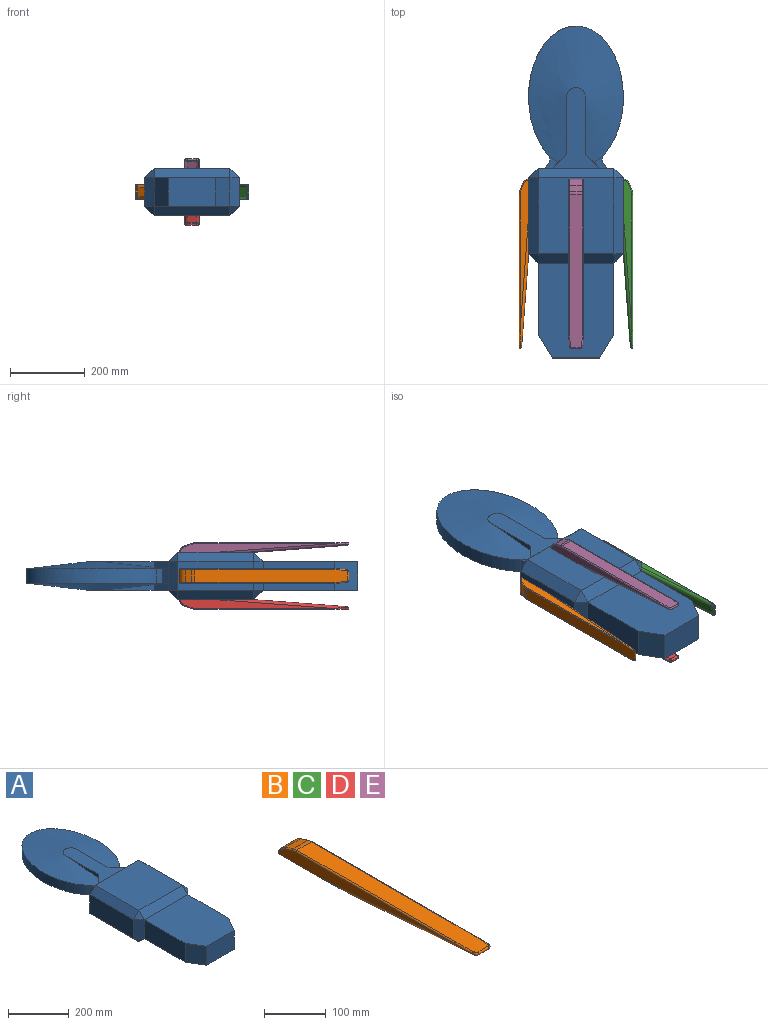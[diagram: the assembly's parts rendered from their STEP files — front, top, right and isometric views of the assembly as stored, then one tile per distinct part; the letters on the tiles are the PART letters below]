
ASSEMBLY  parts=5 mates=3
PART A: 54 faces, bbox 256.2x891.2x129.2 mm
  f0: plane 190.5x76.2mm, normal (1,0,0), area 14516.1mm2, adj f1,f3,f27,f53
  f1: plane 254x203.2mm, normal (0,0,1), area 49193.5mm2, adj f0,f2,f22,f51,f52,f53
  f2: plane 127x76.2mm, normal (0,-1,0), area 9677.4mm2, adj f1,f3,f52,f53
  f3: plane 254x203.2mm, normal (0,0,-1), area 49193.5mm2, adj f0,f2,f33,f51,f52,f53
  f4: plane 36.25x31.4mm, normal (0,0,1), area 482.6mm2, adj f9,f37,f38,f39,f50
  f5: plane 76.2x38.1mm, normal (0,1,0), area 2080.6mm2, adj f7,f8,f14,f18,f19,f34,f46,f49
  f6: plane 36.43x31.41mm, normal (0,0,-1), area 482.7mm2, adj f9,f37,f38,f41,f43
  f7: plane 36.43x31.41mm, normal (0,0,-1), area 482.6mm2, adj f5,f34,f35,f41,f46
  f8: plane 36.25x31.4mm, normal (0,0,1), area 482.7mm2, adj f5,f34,f35,f39,f49
  f9: plane 76.2x38.1mm, normal (0,1,0), area 2080.6mm2, adj f4,f6,f14,f19,f20,f38,f43,f50
  f10: plane 203.2x76.2mm, normal (1,0,0), area 15483.8mm2, adj f17,f18,f27,f28
  f11: plane 203.2x76.2mm, normal (-1,0,0), area 15483.8mm2, adj f20,f21,f29,f30
  f12: plane 203.2x203.2mm, normal (0,0,1), area 41290.2mm2, adj f14,f17,f21,f22
  f13: plane 203.2x203.2mm, normal (0,0,-1), area 41290.2mm2, adj f19,f28,f29,f33
  f14: plane 203.2x25.4mm, normal (0,0.71,0.71), area 7299.2mm2, adj f5,f9,f12,f15,f16,f40
  f15: plane 25.4x25.4mm, normal (0.58,0.58,0.58), area 558.7mm2, adj f14,f17,f18
  f16: plane 25.4x25.4mm, normal (-0.58,0.58,0.58), area 558.7mm2, adj f14,f20,f21
  f17: plane 203.2x25.4mm, normal (0.71,0,0.71), area 7299.2mm2, adj f10,f12,f15,f23
  f18: plane 76.2x25.4mm, normal (0.71,0.71,0), area 2737.2mm2, adj f5,f10,f15,f24
  f19: plane 203.2x25.4mm, normal (0,0.71,-0.71), area 7299.2mm2, adj f5,f9,f13,f24,f25,f42
  f20: plane 76.2x25.4mm, normal (-0.71,0.71,0), area 2737.2mm2, adj f9,f11,f16,f25
  f21: plane 203.2x25.4mm, normal (-0.71,0,0.71), area 7299.2mm2, adj f11,f12,f16,f26
  f22: plane 203.2x25.4mm, normal (0,-0.71,0.71), area 7299.2mm2, adj f1,f12,f23,f26
  f23: plane 25.4x25.4mm, normal (0.58,-0.58,0.58), area 558.7mm2, adj f17,f22,f27
  f24: plane 25.4x25.4mm, normal (0.58,0.58,-0.58), area 558.7mm2, adj f18,f19,f28
  f25: plane 25.4x25.4mm, normal (-0.58,0.58,-0.58), area 558.7mm2, adj f19,f20,f29
  f26: plane 25.4x25.4mm, normal (-0.58,-0.58,0.58), area 558.7mm2, adj f21,f22,f30
  f27: plane 76.2x25.4mm, normal (0.71,-0.71,0), area 2737.2mm2, adj f0,f10,f23,f31
  f28: plane 203.2x25.4mm, normal (0.71,0,-0.71), area 7299.2mm2, adj f10,f13,f24,f31
  f29: plane 203.2x25.4mm, normal (-0.71,0,-0.71), area 7299.2mm2, adj f11,f13,f25,f32
  f30: plane 76.2x25.4mm, normal (-0.71,-0.71,0), area 2737.2mm2, adj f11,f26,f32,f51
  f31: plane 25.4x25.4mm, normal (0.58,-0.58,-0.58), area 558.7mm2, adj f27,f28,f33
  f32: plane 25.4x25.4mm, normal (-0.58,-0.58,-0.58), area 558.7mm2, adj f29,f30,f33
  f33: plane 203.2x25.4mm, normal (0,-0.71,-0.71), area 7299.2mm2, adj f3,f13,f31,f32
  f34: plane 38.1x15.7mm, normal (0.72,0.7,0), area 833.7mm2, adj f5,f7,f8,f35
  f35: plane 38.1x15.7mm, normal (1,0,0), area 598.2mm2, adj f7,f8,f34,f36
  f36: extruded ~349.6x253.9mm, area 32395.3mm2, adj f35,f37,f39,f41
  f37: plane 38.1x15.7mm, normal (-1,0,0), area 598.2mm2, adj f4,f6,f36,f38
  f38: plane 38.1x15.7mm, normal (-0.72,0.7,0), area 833.7mm2, adj f4,f6,f9,f37
  f39: bspline ~375.15x253.9mm, area 65380.2mm2, adj f4,f8,f36,f40,f47,f48,f49,f50
  f40: plane 215.9x127mm, normal (0,0,1), area 12142.5mm2, adj f14,f39,f47,f48,f49,f50
  f41: bspline ~375.15x253.91mm, area 65379.8mm2, adj f6,f7,f36,f42,f43,f44,f45,f46
  f42: plane 215.9x127mm, normal (0,0,-1), area 12142.4mm2, adj f19,f41,f43,f44,f45,f46
  f43: plane 40.3x40.3mm, normal (-0.71,0.71,0), area 960.9mm2, adj f6,f9,f41,f42,f44
  f44: plane 152.4x15.18mm, normal (-1,0,0), area 1054.3mm2, adj f41,f42,f43
  f45: plane 152.4x15.18mm, normal (1,0,0), area 1054.3mm2, adj f41,f42,f46
  f46: plane 40.3x40.3mm, normal (0.71,0.71,0), area 960.9mm2, adj f5,f7,f41,f42,f45
  f47: plane 152.4x15.18mm, normal (1,0,0), area 1054.3mm2, adj f39,f40,f49
  f48: plane 152.4x15.18mm, normal (-1,0,0), area 1054.3mm2, adj f39,f40,f50
  f49: plane 40.3x40.3mm, normal (0.71,0.71,0), area 960.9mm2, adj f5,f8,f39,f40,f47
  f50: plane 40.3x40.3mm, normal (-0.71,0.71,0), area 960.9mm2, adj f4,f9,f39,f40,f48
  f51: plane 190.5x76.2mm, normal (-1,0,0), area 14516.1mm2, adj f1,f3,f30,f52
  f52: plane 76.2x63.5mm, normal (-0.86,-0.51,0), area 5642.8mm2, adj f1,f2,f3,f51
  f53: plane 76.2x63.5mm, normal (0.86,-0.51,0), area 5642.8mm2, adj f0,f1,f2,f3
PART B: 26 faces, bbox 42.2x462.5x34.5 mm
  f0: plane 33.02x17.5mm, normal (0,0.32,0.95), area 609.1mm2, adj f6,f7,f14,f24
  f1: plane 410.78x34.08mm, normal (0,0,1), area 13482.5mm2, adj f6,f16,f17,f18,f19,f20,f21,f22
  f2: plane 243.52x22.86mm, normal (0,-0.07,-1), area 5582.4mm2, adj f3,f8,f9,f11
  f3: plane 203.5x38.4mm, normal (0,0,-1), area 7405.9mm2, adj f2,f4,f5,f7,f9,f11,f13,f25
  f4: plane 403.5x22.86mm, normal (1,0,0), area 5483.9mm2, adj f3,f9,f13,f14,f15,f16
  f5: plane 403.5x22.86mm, normal (-1,0,0), area 5483.9mm2, adj f3,f11,f22,f23,f24,f25
  f6: cylinder r=25.4mm len=33.02mm, axis (-1,0,0), area 269.9mm2, adj f0,f1,f15,f23
  f7: cylinder r=25.4mm len=33.02mm, axis (1,0,0), area 853.2mm2, adj f0,f3,f13,f25
  f8: cylinder r=12.7mm len=22.86mm, axis (-1,0,0), area 167.9mm2, adj f2,f10,f12,f19
  f9: cylinder r=7.62mm len=345.4mm, axis (0,-1,0.07), area 3271.2mm2, adj f2,f3,f4,f10,f17
  f10: torus R=5.08mm, axis (1,0,0), area 38.1mm2, adj f8,f9,f18
  f11: cylinder r=7.62mm len=345.4mm, axis (0,1,-0.07), area 3271.2mm2, adj f2,f3,f5,f12,f21
  f12: torus R=5.08mm, axis (1,0,0), area 38.1mm2, adj f8,f11,f20
  f13: torus R=22.86mm, axis (1,0,0), area 98.1mm2, adj f3,f4,f7,f14
  f14: cylinder r=2.54mm len=18.3mm, axis (0,0.95,-0.32), area 73.6mm2, adj f0,f4,f13,f15
  f15: torus R=22.86mm, axis (1,0,0), area 31.4mm2, adj f4,f6,f14,f16
  f16: cylinder r=2.54mm len=363.89mm, axis (0,1,0), area 1451.9mm2, adj f1,f4,f15,f17
  f17: bspline ~47.14x5.28mm, area 192.4mm2, adj f1,f9,f16,f18
  f18: bspline ~13.4x11.71mm, area 62.4mm2, adj f1,f10,f17,f19
  f19: cylinder r=2.54mm len=22.86mm, axis (-1,0,0), area 144.5mm2, adj f1,f8,f18,f20
  f20: bspline ~14.54x11.71mm, area 62.4mm2, adj f1,f12,f19,f21
  f21: bspline ~47.14x5.28mm, area 192.4mm2, adj f1,f11,f20,f22
  f22: cylinder r=2.54mm len=363.89mm, axis (0,-1,0), area 1451.9mm2, adj f1,f5,f21,f23
  f23: torus R=22.86mm, axis (1,0,0), area 31.4mm2, adj f5,f6,f22,f24
  f24: cylinder r=2.54mm len=18.3mm, axis (0,-0.95,0.32), area 73.6mm2, adj f0,f5,f23,f25
  f25: torus R=22.86mm, axis (1,0,0), area 98.1mm2, adj f3,f5,f7,f24
PART C: same geometry as B
PART D: same geometry as B
PART E: same geometry as B
PLACE A at identity fixed
PLACE B rot(axis=(0,-1,0),90deg) t=(-127,98.09,44.45)mm
PLACE C rot(axis=(0,1,0),90deg) t=(127,98.09,82.55)mm
PLACE D rot(axis=(0,1,0),180deg) t=(19.05,98.09,0)mm
PLACE E t=(-19.05,98.09,127)mm
MATE fastened E.f3 <-> A.f12  axis (0,0,-1) through (0,0,127)mm
MATE fastened C.f3 <-> A.f10  axis (-1,0,0) through (127,0,63.5)mm
MATE fastened B.f3 <-> A.f11  axis (1,0,0) through (-127,0,63.5)mm
